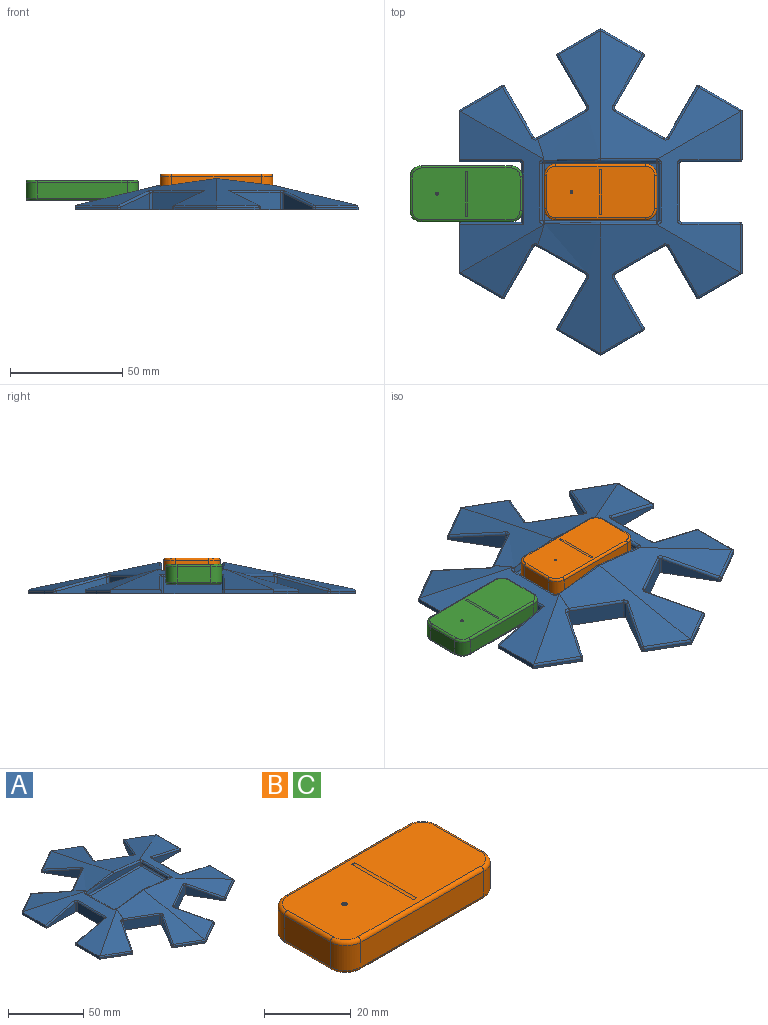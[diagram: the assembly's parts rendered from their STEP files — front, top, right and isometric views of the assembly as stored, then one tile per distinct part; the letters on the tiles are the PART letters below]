
ASSEMBLY  parts=3 mates=1
PART A: 139 faces, bbox 127.9x147.2x15.7 mm
  f0: plane 145.49x126mm, normal (0,0,-1), area 9213mm2, adj f1,f2,f3,f4,f5,f6,f9,f11
  f1: plane 18.94x10.94mm, normal (-0.5,0.87,0), area 26.5mm2, adj f0,f14,f42,f120
  f2: plane 18.94x10.94mm, normal (0.5,0.87,0), area 26.5mm2, adj f0,f16,f50,f115
  f3: plane 21.87x1.21mm, normal (1,0,0), area 26.5mm2, adj f0,f11,f58,f136
  f4: plane 18.94x10.94mm, normal (0.5,-0.87,0), area 26.5mm2, adj f0,f18,f127,f129
  f5: plane 18.94x10.94mm, normal (-0.5,-0.87,0), area 26.5mm2, adj f0,f9,f74,f133
  f6: plane 22.98x2.11mm, normal (-1,0,0), area 45.4mm2, adj f0,f10,f12,f25,f87,f124
  f7: plane 62.23x57.18mm, normal (0.12,-0.2,0.97), area 1273.1mm2, adj f8,f17,f67,f69,f70,f72,f73,f103
  f8: plane 62.23x57.18mm, normal (-0.12,-0.2,0.97), area 1273.1mm2, adj f7,f10,f76,f77,f79,f80,f81,f107
  f9: plane 21.98x2.11mm, normal (-1,0,0), area 43.6mm2, adj f0,f5,f10,f82,f133
  f10: plane 72.19x37.93mm, normal (-0.23,0,0.97), area 1062.8mm2, adj f6,f8,f9,f13,f83,f84,f86,f87
  f11: plane 18.94x10.94mm, normal (0.5,-0.87,0), area 26.5mm2, adj f0,f3,f66,f137
  f12: plane 18.94x10.94mm, normal (-0.5,0.87,0), area 26.5mm2, adj f0,f6,f124,f126
  f13: plane 63.95x58.9mm, normal (-0.12,0.2,0.97), area 1273.1mm2, adj f10,f15,f44,f45,f47,f48,f49,f108
  f14: plane 18.94x10.94mm, normal (0.5,0.87,0), area 26.5mm2, adj f0,f1,f121,f123
  f15: plane 62.23x57.18mm, normal (0.12,0.2,0.97), area 1273.1mm2, adj f13,f17,f52,f53,f55,f56,f57,f104
  f16: plane 21.87x1.21mm, normal (1,0,0), area 26.5mm2, adj f0,f2,f116,f118
  f17: plane 71.86x36.95mm, normal (0.23,0,0.97), area 1029.8mm2, adj f7,f15,f60,f61,f63,f64,f65,f100
  f18: plane 18.94x10.94mm, normal (-0.5,-0.87,0), area 26.5mm2, adj f0,f4,f130,f132
  f19: plane 25x1.54mm, normal (1,0,0), area 38.6mm2, adj f88,f92,f93,f113
  f20: plane 25x1.54mm, normal (-1,0,0), area 38.6mm2, adj f90,f96,f99,f100
  f21: plane 50x4.98mm, normal (0,-1,0), area 174.7mm2, adj f93,f97,f99,f106,f108
  f22: plane 50x4.98mm, normal (0,1,0), area 174.7mm2, adj f88,f90,f91,f105,f107
  f23: plane 50x25mm, normal (0,0,1), area 1250mm2, adj f91,f92,f96,f97
  f24: plane 27x7.64mm, normal (0,1,0), area 119.5mm2, adj f0,f26,f82,f83
  f25: plane 27x7.4mm, normal (0,-1,0), area 113mm2, adj f0,f6,f85,f87
  f26: plane 26.03x7.88mm, normal (-1,0,0), area 204.8mm2, adj f0,f24,f83,f84,f85
  f27: plane 21.65x12.5mm, normal (-0.5,-0.87,0), area 196.9mm2, adj f0,f75,f78,f79
  f28: plane 22.52x13mm, normal (-0.87,0.5,0), area 111.9mm2, adj f0,f78,f81,f132
  f29: plane 22.52x13mm, normal (0.87,-0.5,0), area 111.9mm2, adj f0,f74,f75,f76
  f30: plane 21.65x12.5mm, normal (0.5,-0.87,0), area 196.9mm2, adj f0,f68,f70,f71
  f31: plane 22.52x13mm, normal (-0.87,-0.5,0), area 111.9mm2, adj f0,f66,f67,f68
  f32: plane 22.52x13mm, normal (0.87,0.5,0), area 111.9mm2, adj f0,f71,f73,f127
  f33: plane 25x7.88mm, normal (1,0,0), area 196.9mm2, adj f0,f59,f62,f63
  f34: plane 26x7.4mm, normal (0,-1,0), area 111.9mm2, adj f0,f62,f65,f118
  f35: plane 26x7.4mm, normal (0,1,0), area 111.9mm2, adj f0,f58,f59,f60
  f36: plane 21.65x12.5mm, normal (0.5,0.87,0), area 196.9mm2, adj f0,f51,f54,f55
  f37: plane 22.52x13mm, normal (0.87,-0.5,0), area 111.9mm2, adj f0,f54,f57,f123
  f38: plane 22.52x13mm, normal (-0.87,0.5,0), area 111.9mm2, adj f0,f50,f51,f52
  f39: plane 21.65x12.5mm, normal (-0.5,0.87,0), area 196.9mm2, adj f0,f43,f46,f47
  f40: plane 22.52x13mm, normal (0.87,0.5,0), area 111.9mm2, adj f0,f46,f49,f126
  f41: plane 22.52x13mm, normal (-0.87,-0.5,0), area 111.9mm2, adj f0,f42,f43,f44
  f42: cylinder r=1mm len=1.37mm, axis (0,0,1), area 1.9mm2, adj f0,f1,f41,f119
  f43: cylinder r=1mm len=7.88mm, axis (0,0,-1), area 12mm2, adj f0,f39,f41,f45
  f44: cylinder r=1mm len=23.22mm, axis (0.49,-0.84,0.23), area 42mm2, adj f13,f41,f45,f119
  f45: bspline ~2.73x1.45mm, area 3.2mm2, adj f13,f43,f44,f47
  f46: cylinder r=1mm len=7.88mm, axis (0,0,1), area 12mm2, adj f0,f39,f40,f48
  f47: cylinder r=1mm len=22.04mm, axis (-0.87,-0.5,0), area 33.4mm2, adj f13,f39,f45,f48
  f48: bspline ~2.73x1.45mm, area 3.2mm2, adj f13,f46,f47,f49
  f49: cylinder r=1mm len=22.86mm, axis (-0.49,0.84,-0.23), area 42mm2, adj f13,f40,f48,f125
  f50: cylinder r=1mm len=1.37mm, axis (0,0,1), area 1.9mm2, adj f0,f2,f38,f114
  f51: cylinder r=1mm len=7.88mm, axis (0,0,-1), area 12mm2, adj f0,f36,f38,f53
  f52: cylinder r=1mm len=22.86mm, axis (-0.49,-0.84,0.23), area 42mm2, adj f15,f38,f53,f114
  f53: bspline ~2.73x1.45mm, area 3.2mm2, adj f15,f51,f52,f55
  f54: cylinder r=1mm len=7.88mm, axis (0,0,1), area 12mm2, adj f0,f36,f37,f56
  f55: cylinder r=1mm len=22.04mm, axis (-0.87,0.5,0), area 33.4mm2, adj f15,f36,f53,f56
  f56: bspline ~2.88x1.54mm, area 3.2mm2, adj f15,f54,f55,f57
  f57: cylinder r=1mm len=23.22mm, axis (0.49,0.84,-0.23), area 42mm2, adj f15,f37,f56,f122
  f58: cylinder r=1mm len=1.21mm, axis (0,0,1), area 1.9mm2, adj f0,f3,f35,f135
  f59: cylinder r=1mm len=7.88mm, axis (0,0,-1), area 12mm2, adj f0,f33,f35,f61
  f60: cylinder r=1mm len=26.23mm, axis (-0.97,0,0.23), area 42mm2, adj f17,f35,f61,f135
  f61: bspline ~2x2mm, area 3.2mm2, adj f17,f59,f60,f63
  f62: cylinder r=1mm len=7.88mm, axis (0,0,1), area 12mm2, adj f0,f33,f34,f64
  f63: cylinder r=1mm len=25mm, axis (0,1,0), area 33.4mm2, adj f17,f33,f61,f64
  f64: bspline ~2x2mm, area 3.2mm2, adj f17,f62,f63,f65
  f65: cylinder r=1mm len=26.23mm, axis (0.97,0,-0.23), area 42mm2, adj f17,f34,f64,f117
  f66: cylinder r=1mm len=1.37mm, axis (0,0,-1), area 1.9mm2, adj f0,f11,f31,f138
  f67: cylinder r=1mm len=22.86mm, axis (0.49,-0.84,-0.23), area 42mm2, adj f7,f31,f69,f138
  f68: cylinder r=1mm len=7.88mm, axis (0,0,1), area 12mm2, adj f0,f30,f31,f69
  f69: bspline ~2.73x1.45mm, area 3.2mm2, adj f7,f67,f68,f70
  f70: cylinder r=1mm len=22.04mm, axis (0.87,0.5,0), area 33.4mm2, adj f7,f30,f69,f72
  f71: cylinder r=1mm len=7.88mm, axis (0,0,-1), area 12mm2, adj f0,f30,f32,f72
  f72: bspline ~2.73x1.45mm, area 3.2mm2, adj f7,f70,f71,f73
  f73: cylinder r=1mm len=23.22mm, axis (-0.49,0.84,0.23), area 42mm2, adj f7,f32,f72,f128
  f74: cylinder r=1mm len=1.37mm, axis (0,0,1), area 1.9mm2, adj f0,f5,f29,f134
  f75: cylinder r=1mm len=7.88mm, axis (0,0,-1), area 12mm2, adj f0,f27,f29,f77
  f76: cylinder r=1mm len=22.86mm, axis (0.49,0.84,0.23), area 42mm2, adj f8,f29,f77,f134
  f77: bspline ~2.73x1.45mm, area 3.2mm2, adj f8,f75,f76,f79
  f78: cylinder r=1mm len=7.88mm, axis (0,0,1), area 12mm2, adj f0,f27,f28,f80
  f79: cylinder r=1mm len=22.04mm, axis (0.87,-0.5,0), area 33.4mm2, adj f8,f27,f77,f80
  f80: bspline ~2.73x1.45mm, area 3.2mm2, adj f8,f78,f79,f81
  f81: cylinder r=1mm len=23.22mm, axis (-0.49,-0.84,-0.23), area 42mm2, adj f8,f28,f80,f131
  f82: cylinder r=1mm len=2mm, axis (0,0,-1), area 2.5mm2, adj f0,f9,f24,f83
  f83: cylinder r=1mm len=29mm, axis (-0.97,0,-0.23), area 45mm2, adj f10,f24,f26,f82,f84
  f84: cylinder r=1mm len=27mm, axis (0,-1,0), area 35.5mm2, adj f10,f26,f83,f86
  f85: cylinder r=1mm len=7.88mm, axis (0,0,-1), area 12mm2, adj f0,f25,f26,f86
  f86: bspline ~2x2mm, area 3.2mm2, adj f10,f84,f85,f87
  f87: cylinder r=1mm len=27.23mm, axis (0.97,0,0.23), area 43.4mm2, adj f6,f10,f25,f86
  f88: cylinder r=1mm len=2.01mm, axis (0,0,1), area 2.7mm2, adj f19,f22,f89,f109,f111
  f89: sphere r=1mm, area 1.6mm2, adj f88,f91,f92
  f90: cylinder r=1mm len=2.01mm, axis (0,0,-1), area 2.7mm2, adj f20,f22,f94,f101,f103
  f91: cylinder r=1mm len=50mm, axis (1,0,0), area 78.5mm2, adj f22,f23,f89,f94
  f92: cylinder r=1mm len=25mm, axis (0,-1,0), area 39.3mm2, adj f19,f23,f89,f95
  f93: cylinder r=1mm len=2.01mm, axis (0,0,-1), area 2.7mm2, adj f19,f21,f95,f110,f112
  f94: sphere r=1mm, area 1.6mm2, adj f90,f91,f96
  f95: sphere r=1mm, area 2.1mm2, adj f92,f93,f97
  f96: cylinder r=1mm len=25mm, axis (0,1,0), area 39.3mm2, adj f20,f23,f94,f98
  f97: cylinder r=1mm len=50mm, axis (-1,0,0), area 78.5mm2, adj f21,f23,f95,f98
  f98: sphere r=1mm, area 1mm2, adj f96,f97,f99
  f99: cylinder r=1mm len=2.01mm, axis (0,0,1), area 2.7mm2, adj f20,f21,f98,f102,f104
  f100: cylinder r=1mm len=25mm, axis (0,-1,0), area 45.1mm2, adj f17,f20,f101,f102
  f101: bspline ~2.21x2mm, area 3.6mm2, adj f17,f90,f100,f103
  f102: bspline ~2.21x2mm, area 3.6mm2, adj f17,f99,f100,f104
  f103: bspline ~1.21x1.02mm, area 0.2mm2, adj f7,f17,f90,f101,f105
  f104: bspline ~1.21x1.02mm, area 0.2mm2, adj f15,f17,f99,f102,f106
  f105: cylinder r=1mm len=25.23mm, axis (-0.99,0,0.12), area 44.7mm2, adj f7,f22,f103,f107
  f106: cylinder r=1mm len=25.23mm, axis (0.99,0,-0.12), area 44.7mm2, adj f15,f21,f104,f108
  f107: cylinder r=1mm len=25.23mm, axis (-0.99,0,-0.12), area 44.7mm2, adj f8,f22,f105
  f108: cylinder r=1mm len=25.23mm, axis (0.99,0,0.12), area 44.7mm2, adj f13,f21,f106
  f109: bspline ~1.21x1.02mm, area 0.2mm2, adj f8,f10,f88,f111
  f110: bspline ~1.28x1.27mm, area 0.1mm2, adj f10,f13,f93,f112
  f111: bspline ~2.21x2mm, area 3.6mm2, adj f10,f88,f109,f113
  f112: bspline ~2.21x2mm, area 3.6mm2, adj f10,f93,f110,f113
  f113: cylinder r=1mm len=25mm, axis (0,1,0), area 45.1mm2, adj f10,f19,f111,f112
  f114: sphere r=1mm, area 0.9mm2, adj f50,f52,f115
  f115: cylinder r=1mm len=19.33mm, axis (-0.87,0.5,0), area 28.9mm2, adj f2,f15,f114,f116
  f116: cylinder r=1mm len=21.87mm, axis (0,1,0), area 28.9mm2, adj f16,f17,f115,f117
  f117: sphere r=1mm, area 1mm2, adj f65,f116,f118
  f118: cylinder r=1mm len=1.21mm, axis (0,0,-1), area 1.9mm2, adj f0,f16,f34,f117
  f119: sphere r=1mm, area 0.9mm2, adj f42,f44,f120
  f120: cylinder r=1mm len=19.33mm, axis (-0.87,-0.5,0), area 28.9mm2, adj f1,f13,f119,f121
  f121: cylinder r=1mm len=19.33mm, axis (-0.87,0.5,0), area 28.9mm2, adj f14,f15,f120,f122
  f122: sphere r=1mm, area 0.9mm2, adj f57,f121,f123
  f123: cylinder r=1mm len=1.37mm, axis (0,0,-1), area 1.9mm2, adj f0,f14,f37,f122
  f124: cylinder r=1mm len=19.52mm, axis (-0.87,-0.5,0), area 29.3mm2, adj f6,f10,f12,f13,f125
  f125: sphere r=1mm, area 1mm2, adj f49,f124,f126
  f126: cylinder r=1mm len=1.37mm, axis (0,0,-1), area 1.9mm2, adj f0,f12,f40,f125
  f127: cylinder r=1mm len=1.37mm, axis (0,0,1), area 1.9mm2, adj f0,f4,f32,f128
  f128: sphere r=1mm, area 1.8mm2, adj f73,f127,f129
  f129: cylinder r=1mm len=19.33mm, axis (0.87,0.5,0), area 28.9mm2, adj f4,f7,f128,f130
  f130: cylinder r=1mm len=19.33mm, axis (-0.87,0.5,0), area 28.9mm2, adj f8,f18,f129,f131
  f131: sphere r=1mm, area 1.8mm2, adj f81,f130,f132
  f132: cylinder r=1mm len=1.37mm, axis (0,0,-1), area 1.9mm2, adj f0,f18,f28,f131
  f133: cylinder r=1mm len=19.52mm, axis (-0.87,0.5,0), area 29.3mm2, adj f5,f8,f9,f10,f134
  f134: sphere r=1mm, area 0.9mm2, adj f74,f76,f133
  f135: sphere r=1mm, area 0.9mm2, adj f58,f60,f136
  f136: cylinder r=1mm len=21.87mm, axis (0,1,0), area 28.9mm2, adj f3,f17,f135,f137
  f137: cylinder r=1mm len=19.33mm, axis (0.87,0.5,0), area 28.9mm2, adj f7,f11,f136,f138
  f138: sphere r=1mm, area 0.9mm2, adj f66,f67,f137
PART B: 31 faces, bbox 50.8x25.8x9 mm
  f0: plane 48x23mm, normal (0,0,1), area 1069mm2, adj f18,f19,f20,f21,f22,f23,f24,f25
  f1: plane 15x7mm, normal (1,0,0), area 105mm2, adj f6,f9,f16,f23
  f2: plane 40x7mm, normal (0,1,0), area 280mm2, adj f6,f7,f15,f24
  f3: plane 15x7mm, normal (-1,0,0), area 105mm2, adj f7,f8,f11,f20
  f4: plane 40x7mm, normal (0,-1,0), area 280mm2, adj f8,f9,f12,f19
  f5: plane 48x23mm, normal (0,0,-1), area 1090.3mm2, adj f10,f11,f12,f13,f14,f15,f16,f17
  f6: cylinder r=5mm len=7mm, axis (0,0,-1), area 55mm2, adj f1,f2,f17,f25
  f7: cylinder r=5mm len=7mm, axis (0,0,1), area 55mm2, adj f2,f3,f13,f22
  f8: cylinder r=5mm len=7mm, axis (0,0,-1), area 55mm2, adj f3,f4,f10,f18
  f9: cylinder r=5mm len=7mm, axis (0,0,1), area 55mm2, adj f1,f4,f14,f21
  f10: torus R=4mm, axis (0,0,1), area 11.4mm2, adj f5,f8,f11,f12
  f11: cylinder r=1mm len=15mm, axis (0,1,0), area 23.6mm2, adj f3,f5,f10,f13
  f12: cylinder r=1mm len=40mm, axis (-1,0,0), area 62.8mm2, adj f4,f5,f10,f14
  f13: torus R=4mm, axis (0,0,1), area 11.4mm2, adj f5,f7,f11,f15
  f14: torus R=4mm, axis (0,0,1), area 11.4mm2, adj f5,f9,f12,f16
  f15: cylinder r=1mm len=40mm, axis (1,0,0), area 62.8mm2, adj f2,f5,f13,f17
  f16: cylinder r=1mm len=15mm, axis (0,-1,0), area 23.6mm2, adj f1,f5,f14,f17
  f17: torus R=4mm, axis (0,0,1), area 11.4mm2, adj f5,f6,f15,f16
  f18: torus R=4mm, axis (0,0,1), area 11.4mm2, adj f0,f8,f19,f20
  f19: cylinder r=1mm len=40mm, axis (1,0,0), area 62.8mm2, adj f0,f4,f18,f21
  f20: cylinder r=1mm len=15mm, axis (0,-1,0), area 23.6mm2, adj f0,f3,f18,f22
  f21: torus R=4mm, axis (0,0,1), area 11.4mm2, adj f0,f9,f19,f23
  f22: torus R=4mm, axis (0,0,1), area 11.4mm2, adj f0,f7,f20,f24
  f23: cylinder r=1mm len=15mm, axis (0,1,0), area 23.6mm2, adj f0,f1,f21,f25
  f24: cylinder r=1mm len=40mm, axis (-1,0,0), area 62.8mm2, adj f0,f2,f22,f25
  f25: torus R=4mm, axis (0,0,1), area 11.4mm2, adj f0,f6,f23,f24
  f26: cylinder r=0.8mm len=20mm, axis (0,-1,0), area 21.6mm2, adj f0,f27,f28
  f27: plane 1x0.18mm, normal (0,-1,0), area 0.1mm2, adj f0,f26
  f28: plane 1x0.18mm, normal (0,1,0), area 0.1mm2, adj f0,f26
  f29: sphere r=0.87mm, area 0.5mm2, adj f30
  f30: torus R=0.64mm, axis (0,0,1), area 0.8mm2, adj f0,f29
PART C: same geometry as B
PLACE A t=(-4.04,-0.99,-8.91)mm
PLACE B t=(-4.04,-0.99,7.09)mm
PLACE C t=(-63.88,-1.83,4.34)mm
MATE fastened B.f5 <-> A.f23  axis (0,0,-1) through (-4.04,-0.99,-1.91)mm
